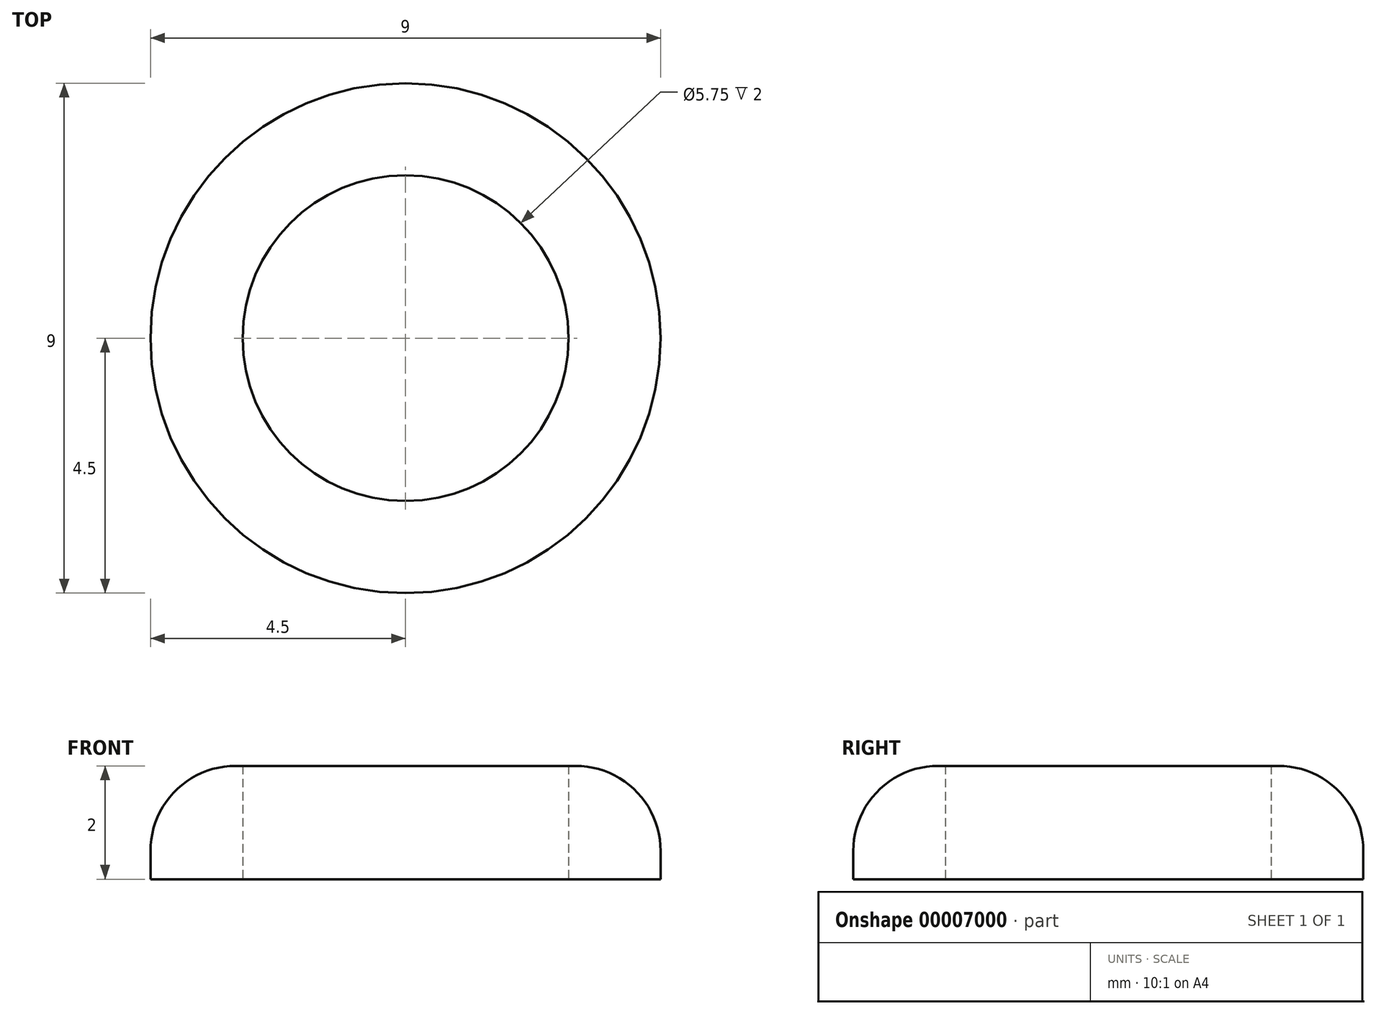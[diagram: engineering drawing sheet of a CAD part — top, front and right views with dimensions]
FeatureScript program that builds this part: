
annotation { "Feature Type Name" : "Feature", "Feature Type Description" : "" }
export const myFeature = defineFeature(function(context is Context, id is Id, definition is map)
    precondition{}
    {
        {
            var Q0;
            Q0=qCreatedBy(makeId("Top.planeOp"),FACE);
            var sketch = newSketch(context, id + "F0", { "sketchPlane" : qUnion([Q0])});
            skCircle(sketch, "E0", {"center": v(0, 0) * mm, "radius": 2.88 * mm});
            skCircle(sketch, "E1", {"center": v(0, 0) * mm, "radius": 4.5 * mm});
            skSolve(sketch);
        }
        {
            var Q0;
            Q0 = qSketchRegion(id + "F0", true);
            extrude(context, id + "F1", {"entities" : qUnion([Q0]), "depth" : 2 * mm});
        }
        {
            var Q0;
            Q0=makeQuery(id+"F1.opExtrude","CAP_EDGE",EDGE,{"disambiguationData":[OSD([sQuery(id+"F0.wireOp",EDGE,"E1")])],"isStart":false});
            fillet(context, id + "F2", {"entities" : qUnion([Q0]), "radius" : 1.5 * mm, "tangentPropagation" : true, "allowEdgeOverflow" : false});
        }
    });
